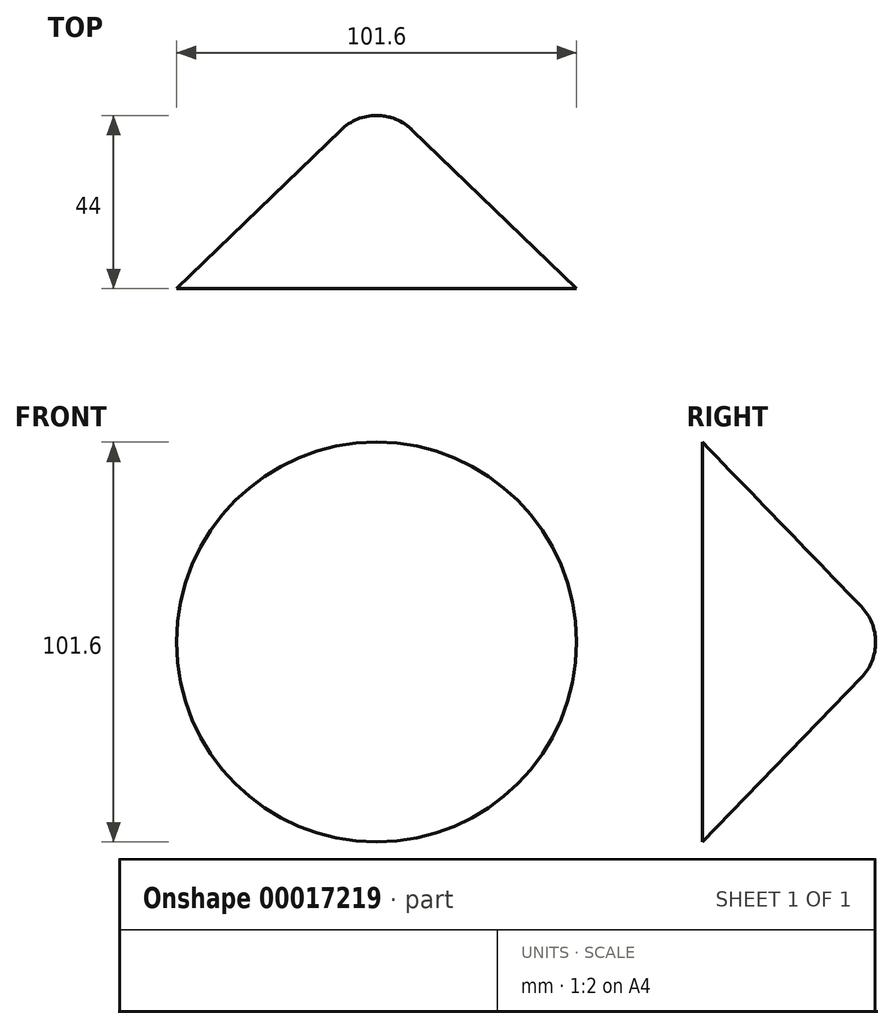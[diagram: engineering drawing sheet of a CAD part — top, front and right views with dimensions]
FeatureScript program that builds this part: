
annotation { "Feature Type Name" : "Feature", "Feature Type Description" : "" }
export const myFeature = defineFeature(function(context is Context, id is Id, definition is map)
    precondition{}
    {
        {
            var Q0;
            Q0=qCreatedBy(makeId("Front.planeOp"),FACE);
            cPlane(context, id + "F0", {"entities" : qUnion([Q0]), "cplaneType" : CPlaneType.OFFSET, "offset" : 31 * mm, "oppositeDirection" : true, "width" : 150 * mm, "height" : 150 * mm});
        }
        {
            var Q0;
            Q0=qCreatedBy(makeId("Top.planeOp"),FACE);
            var sketch = newSketch(context, id + "F1", { "sketchPlane" : qUnion([Q0])});
            skLineSegment(sketch, "E0", {"start": v(0, 0) * mm, "end": v(0, 31) * mm, "construction": true});
            skArc(sketch, "E1", {"start": v(9.03, 40.35) * mm, "mid": v(4.87, 43.05) * mm, "end": v(0, 44) * mm});
            skLineSegment(sketch, "E2", {"start": v(0, 0) * mm, "end": v(50.8, 0) * mm});
            skLineSegment(sketch, "E3", {"start": v(50.8, 0) * mm, "end": v(9.03, 40.35) * mm});
            skLineSegment(sketch, "E4", {"start": v(0, 0) * mm, "end": v(-50.8, 0) * mm, "construction": true});
            skLineSegment(sketch, "E5", {"start": v(0, 0) * mm, "end": v(0, 44) * mm});
            skSolve(sketch);
        }
        {
            var Q0;
            Q0=sQuery(id+"F1.wireOp",EDGE,"E2");
            var Q1;
            Q1=sQuery(id+"F1.wireOp",EDGE,"E3");
            var Q2;
            Q2=sQuery(id+"F1.wireOp",EDGE,"E1");
            var Q3;
            Q3=sQuery(id+"F1.wireOp",EDGE,"E5");
            revolve(context, id + "F2", {"bodyType" : ToolBodyType.SURFACE, "surfaceEntities" : qUnion([Q0, Q1, Q2]), "axis" : qUnion([Q3]), "revolveType" : RevolveType.ONE_DIRECTION, "angle" : 360 * degree});
        }
    });
